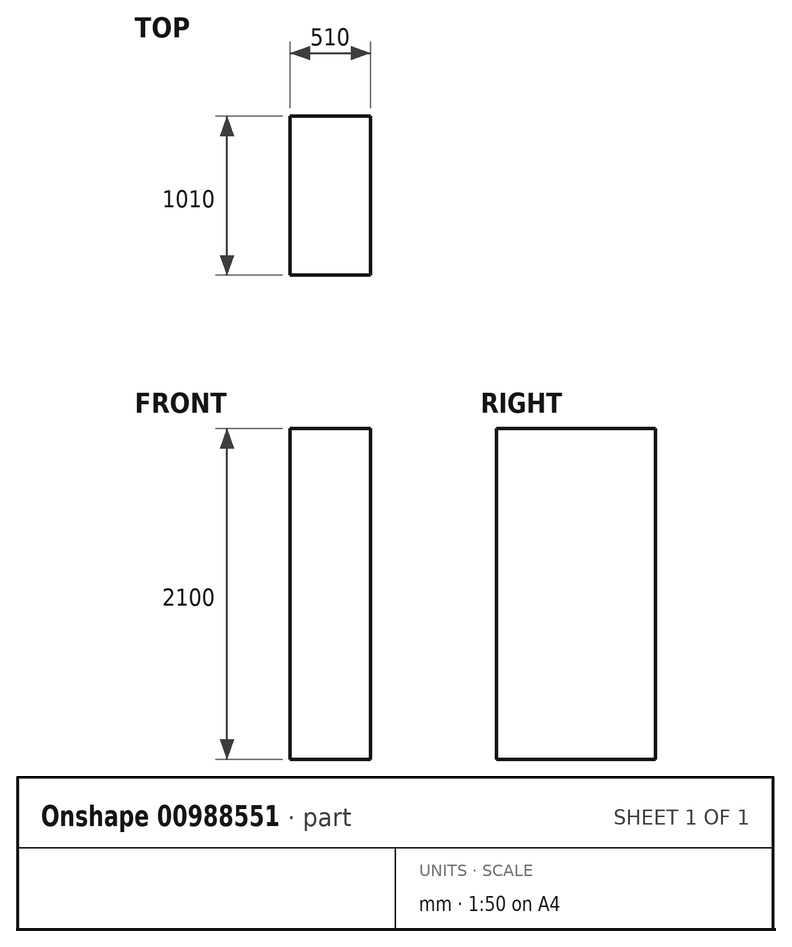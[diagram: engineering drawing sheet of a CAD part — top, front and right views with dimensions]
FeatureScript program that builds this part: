
annotation { "Feature Type Name" : "Feature", "Feature Type Description" : "" }
export const myFeature = defineFeature(function(context is Context, id is Id, definition is map)
    precondition{}
    {
        {
            var Q0;
            Q0=qCreatedBy(makeId("Top.planeOp"),FACE);
            var sketch = newSketch(context, id + "F0", { "sketchPlane" : qUnion([Q0])});
            skLineSegment(sketch, "E0.bottom", {"start": v(0, 0) * mm, "end": v(510, 0) * mm});
            skLineSegment(sketch, "E0.top", {"start": v(0, 1010) * mm, "end": v(510, 1010) * mm});
            skLineSegment(sketch, "E0.left", {"start": v(0, 0) * mm, "end": v(0, 1010) * mm});
            skLineSegment(sketch, "E0.right", {"start": v(510, 0) * mm, "end": v(510, 1010) * mm});
            skSolve(sketch);
        }
        {
            var Q0;
            Q0=makeQuery(id+"F0.imprint","IMPRINT",FACE,{"disambiguationData":[TD([[makeQuery(id+"F0.imprint","IMPRINT",EDGE,{"derivedFrom":sQuery(id+"F0.wireOp",EDGE,"E0.bottom")}),1.0]])]});
            extrude(context, id + "F1", {"entities" : qUnion([Q0]), "depth" : 2100 * mm, "offsetDistance" : 25 * mm});
        }
    });
